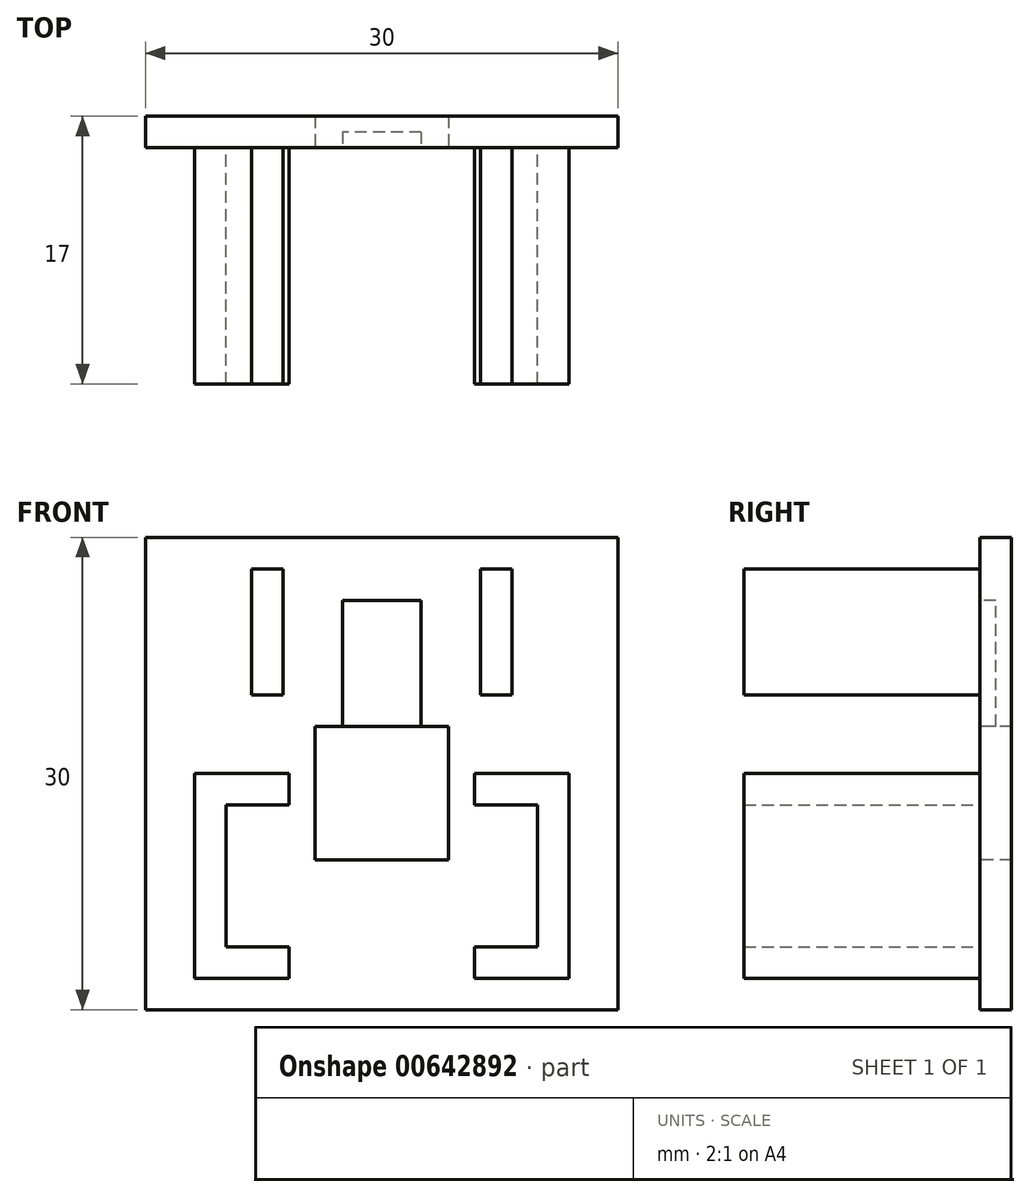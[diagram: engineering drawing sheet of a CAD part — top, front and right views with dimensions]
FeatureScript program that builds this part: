
annotation { "Feature Type Name" : "Feature", "Feature Type Description" : "" }
export const myFeature = defineFeature(function(context is Context, id is Id, definition is map)
    precondition{}
    {
        {
            var Q0;
            Q0=qCreatedBy(makeId("Front.planeOp"),FACE);
            var sketch = newSketch(context, id + "F0", { "sketchPlane" : qUnion([Q0])});
            skLineSegment(sketch, "E0.bottom", {"start": v(15, -15) * mm, "end": v(-15, -15) * mm});
            skLineSegment(sketch, "E0.top", {"start": v(15, 15) * mm, "end": v(-15, 15) * mm});
            skLineSegment(sketch, "E0.left", {"start": v(15, -15) * mm, "end": v(15, 15) * mm});
            skLineSegment(sketch, "E0.right", {"start": v(-15, -15) * mm, "end": v(-15, 15) * mm});
            skPoint(sketch, "E0.middle", {"position": v(0, 0) * mm});
            skSolve(sketch);
        }
        {
            var Q0;
            Q0=makeQuery(id+"F0.imprint","IMPRINT",FACE,{"disambiguationData":[TD([[makeQuery(id+"F0.imprint","IMPRINT",EDGE,{"derivedFrom":sQuery(id+"F0.wireOp",EDGE,"E0.bottom")}),-1.0]])]});
            extrude(context, id + "F1", {"entities" : qUnion([Q0]), "depth" : 2 * mm, "offsetDistance" : 25 * mm});
        }
        {
            var Q0;
            Q0=makeQuery(id+"F1.opExtrude","CAP_FACE",FACE,{"disambiguationData":[OSD([sQuery(id+"F0.wireOp",EDGE,"E0.bottom"),sQuery(id+"F0.wireOp",EDGE,"E0.top"),sQuery(id+"F0.wireOp",EDGE,"E0.left"),sQuery(id+"F0.wireOp",EDGE,"E0.right")])],"isStart":false});
            var sketch = newSketch(context, id + "F2", { "sketchPlane" : qUnion([Q0])});
            skLineSegment(sketch, "E1", {"start": v(5.9, -13) * mm, "end": v(5.9, -11) * mm});
            skLineSegment(sketch, "E2", {"start": v(5.9, -11) * mm, "end": v(9.9, -11) * mm});
            skLineSegment(sketch, "E3", {"start": v(9.9, -11) * mm, "end": v(9.9, -2) * mm});
            skLineSegment(sketch, "E4", {"start": v(9.9, -2) * mm, "end": v(5.9, -2) * mm});
            skLineSegment(sketch, "E5", {"start": v(5.9, -2) * mm, "end": v(5.9, 0) * mm});
            skLineSegment(sketch, "E6", {"start": v(5.9, 0) * mm, "end": v(11.9, 0) * mm});
            skLineSegment(sketch, "E7", {"start": v(11.9, 0) * mm, "end": v(11.9, -13) * mm});
            skLineSegment(sketch, "E8", {"start": v(11.9, -13) * mm, "end": v(5.9, -13) * mm});
            skLineSegment(sketch, "E9.MirrorCS", {"start": v(-5.9, -2) * mm, "end": v(-5.9, 0) * mm});
            skLineSegment(sketch, "E10.MirrorCS", {"start": v(-5.9, -13) * mm, "end": v(-5.9, -11) * mm});
            skLineSegment(sketch, "E11.MirrorCS", {"start": v(-5.9, -11) * mm, "end": v(-9.9, -11) * mm});
            skLineSegment(sketch, "E12.MirrorCS", {"start": v(-9.9, -11) * mm, "end": v(-9.9, -2) * mm});
            skLineSegment(sketch, "E13.MirrorCS", {"start": v(-5.9, 0) * mm, "end": v(-11.9, 0) * mm});
            skLineSegment(sketch, "E14.MirrorCS", {"start": v(-11.9, 0) * mm, "end": v(-11.9, -13) * mm});
            skLineSegment(sketch, "E15.MirrorCS", {"start": v(-9.9, -2) * mm, "end": v(-5.9, -2) * mm});
            skLineSegment(sketch, "E16.MirrorCS", {"start": v(-11.9, -13) * mm, "end": v(-5.9, -13) * mm});
            skSolve(sketch);
        }
        {
            var Q0;
            Q0=makeQuery(id+"F2.imprint","IMPRINT",FACE,{"disambiguationData":[TD([[makeQuery(id+"F2.imprint","IMPRINT",EDGE,{"derivedFrom":sQuery(id+"F2.wireOp",EDGE,"E1")}),-1.0]])]});
            var Q1;
            Q1=makeQuery(id+"F2.imprint","IMPRINT",FACE,{"disambiguationData":[TD([[makeQuery(id+"F2.imprint","IMPRINT",EDGE,{"derivedFrom":sQuery(id+"F2.wireOp",EDGE,"E9.MirrorCS")}),1.0]])]});
            extrude(context, id + "F3", {"entities" : qUnion([Q0, Q1]), "operationType" : NewBodyOperationType.ADD, "depth" : 15 * mm, "offsetDistance" : 25 * mm});
        }
        {
            var Q0;
            Q0=makeQuery(id+"F1.opExtrude","CAP_FACE",FACE,{"disambiguationData":[OSD([sQuery(id+"F0.wireOp",EDGE,"E0.bottom"),sQuery(id+"F0.wireOp",EDGE,"E0.top"),sQuery(id+"F0.wireOp",EDGE,"E0.left"),sQuery(id+"F0.wireOp",EDGE,"E0.right")])],"isStart":false});
            var sketch = newSketch(context, id + "F4", { "sketchPlane" : qUnion([Q0])});
            skLineSegment(sketch, "E17.bottom", {"start": v(4.25, -5.5) * mm, "end": v(-4.25, -5.5) * mm});
            skLineSegment(sketch, "E17.top", {"start": v(4.25, 3) * mm, "end": v(-4.25, 3) * mm});
            skLineSegment(sketch, "E17.left", {"start": v(4.25, -5.5) * mm, "end": v(4.25, 3) * mm});
            skLineSegment(sketch, "E17.right", {"start": v(-4.25, -5.5) * mm, "end": v(-4.25, 3) * mm});
            skPoint(sketch, "E17.middle", {"position": v(0, 0) * mm});
            skSolve(sketch);
        }
        {
            var Q0;
            Q0=makeQuery(id+"F4.imprint","IMPRINT",FACE,{"disambiguationData":[TD([[makeQuery(id+"F4.imprint","IMPRINT",EDGE,{"derivedFrom":sQuery(id+"F4.wireOp",EDGE,"E17.bottom")}),-1.0]])]});
            extrude(context, id + "F5", {"entities" : qUnion([Q0]), "operationType" : NewBodyOperationType.REMOVE, "oppositeDirection" : true, "depth" : 25 * mm, "offsetDistance" : 25 * mm});
        }
        {
            var Q0;
            Q0=makeQuery(id+"F1.opExtrude","CAP_FACE",FACE,{"disambiguationData":[OSD([sQuery(id+"F0.wireOp",EDGE,"E0.bottom"),sQuery(id+"F0.wireOp",EDGE,"E0.top"),sQuery(id+"F0.wireOp",EDGE,"E0.left"),sQuery(id+"F0.wireOp",EDGE,"E0.right")])],"isStart":false});
            var sketch = newSketch(context, id + "F6", { "sketchPlane" : qUnion([Q0])});
            skLineSegment(sketch, "E18.bottom", {"start": v(6.26, 13) * mm, "end": v(8.26, 13) * mm});
            skLineSegment(sketch, "E18.top", {"start": v(6.26, 5) * mm, "end": v(8.26, 5) * mm});
            skLineSegment(sketch, "E18.left", {"start": v(6.26, 13) * mm, "end": v(6.26, 5) * mm});
            skLineSegment(sketch, "E18.right", {"start": v(8.26, 13) * mm, "end": v(8.26, 5) * mm});
            skLineSegment(sketch, "E19.MirrorCS", {"start": v(-6.26, 13) * mm, "end": v(-6.26, 5) * mm});
            skLineSegment(sketch, "E20.MirrorCS", {"start": v(-6.26, 13) * mm, "end": v(-8.26, 13) * mm});
            skLineSegment(sketch, "E21.MirrorCS", {"start": v(-8.26, 13) * mm, "end": v(-8.26, 5) * mm});
            skLineSegment(sketch, "E22.MirrorCS", {"start": v(-6.26, 5) * mm, "end": v(-8.26, 5) * mm});
            skSolve(sketch);
        }
        {
            var Q0;
            Q0=makeQuery(id+"F6.imprint","IMPRINT",FACE,{"disambiguationData":[TD([[makeQuery(id+"F6.imprint","IMPRINT",EDGE,{"derivedFrom":sQuery(id+"F6.wireOp",EDGE,"E19.MirrorCS")}),-1.0]])]});
            var Q1;
            Q1=makeQuery(id+"F6.imprint","IMPRINT",FACE,{"disambiguationData":[TD([[makeQuery(id+"F6.imprint","IMPRINT",EDGE,{"derivedFrom":sQuery(id+"F6.wireOp",EDGE,"E18.bottom")}),-1.0]])]});
            extrude(context, id + "F7", {"entities" : qUnion([Q0, Q1]), "operationType" : NewBodyOperationType.ADD, "depth" : 15 * mm, "offsetDistance" : 25 * mm});
        }
        {
            var Q0;
            Q0=makeQuery(id+"F1.opExtrude","CAP_FACE",FACE,{"disambiguationData":[OSD([sQuery(id+"F0.wireOp",EDGE,"E0.bottom"),sQuery(id+"F0.wireOp",EDGE,"E0.top"),sQuery(id+"F0.wireOp",EDGE,"E0.left"),sQuery(id+"F0.wireOp",EDGE,"E0.right")])],"isStart":false});
            var sketch = newSketch(context, id + "F8", { "sketchPlane" : qUnion([Q0])});
            skLineSegment(sketch, "E23.bottom", {"start": v(-2.5, 3) * mm, "end": v(2.5, 3) * mm});
            skLineSegment(sketch, "E23.top", {"start": v(-2.5, 11) * mm, "end": v(2.5, 11) * mm});
            skLineSegment(sketch, "E23.left", {"start": v(-2.5, 3) * mm, "end": v(-2.5, 11) * mm});
            skLineSegment(sketch, "E23.right", {"start": v(2.5, 3) * mm, "end": v(2.5, 11) * mm});
            skSolve(sketch);
        }
        {
            var Q0;
            Q0 = qSketchRegion(id + "F8", true);
            extrude(context, id + "F9", {"entities" : qUnion([Q0]), "operationType" : NewBodyOperationType.REMOVE, "oppositeDirection" : true, "depth" : 1 * mm, "offsetDistance" : 25 * mm});
        }
    });
